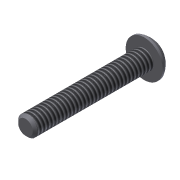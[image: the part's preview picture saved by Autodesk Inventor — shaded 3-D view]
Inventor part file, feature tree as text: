
AUTODESK INVENTOR PART (.ipt)
format: ipt  version: 2013 (Build 170138000, 138)  size: 115,200 bytes
history: native  units: in
note: dims shown in document units (in); Inventor stores cm internally (conversion verified against a paired STEP export)
features: sketch x3, extrude x2, revolve x1, chamfer x1, thread x1
ambient origin geometry x8: Origin, YZ Plane, XZ Plane, XY Plane, X Axis, Y Axis, Z Axis, Center Point
bodies: Solid1 (feature_tree)
feature tree (8):
  extrude  "Extrusion1"  Depth=1.0in TaperAngle=0.0deg
  revolve  "Revolution1"  [1 undecoded]
  extrude  "Extrusion2"  Depth=0.0938in
  chamfer  "Chamfer1"  Distance=0.0625in
  thread  "Thread1"  [1 undecoded]
  sketch  "Sketch1"  dims[d0=0.164in d1=1.0in d2=0.0in]
  sketch  "Sketch2"  dims[d3=0.087in d6=0.08in]
  sketch  "Sketch3"  dims[d7=90.0deg d8=0.0938in d9=0.0625in d10=0.0in d13=0.02in d14=0.125in d15=45.0deg d16=1.0in d17=0.0in d19=0.156in]
note: 2 required parameter values undecoded (feature->parameter linkage not recoverable at this tier; creation-order binding heuristic only, values carry confidence <= 0.55)